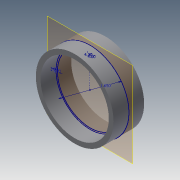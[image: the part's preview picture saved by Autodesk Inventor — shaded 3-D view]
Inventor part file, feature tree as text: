
AUTODESK INVENTOR PART (.ipt)
format: ipt  version: 2015 (Build 190159000, 159)  size: 95,744 bytes
history: native  units: in
note: dims shown in document units (in); Inventor stores cm internally (conversion verified against a paired STEP export)
features: sketch x2, extrude x1, plane x1
ambient origin geometry x8: Origin, YZ Plane, XZ Plane, XY Plane, X Axis, Y Axis, Z Axis, Center Point
bodies: Body1 (feature_tree)
feature tree (4):
  sketch  "Sketch2"  dims[d4=1.65in d5=0.1in]
  extrude  "Extrusion2"  Depth=0.1in
  plane  "Work Plane1"
  sketch  "Sketch4"  dims[d6=0.03in d7=0.65in d8=0.0in d11=0.0275in d12=0.0275in]
